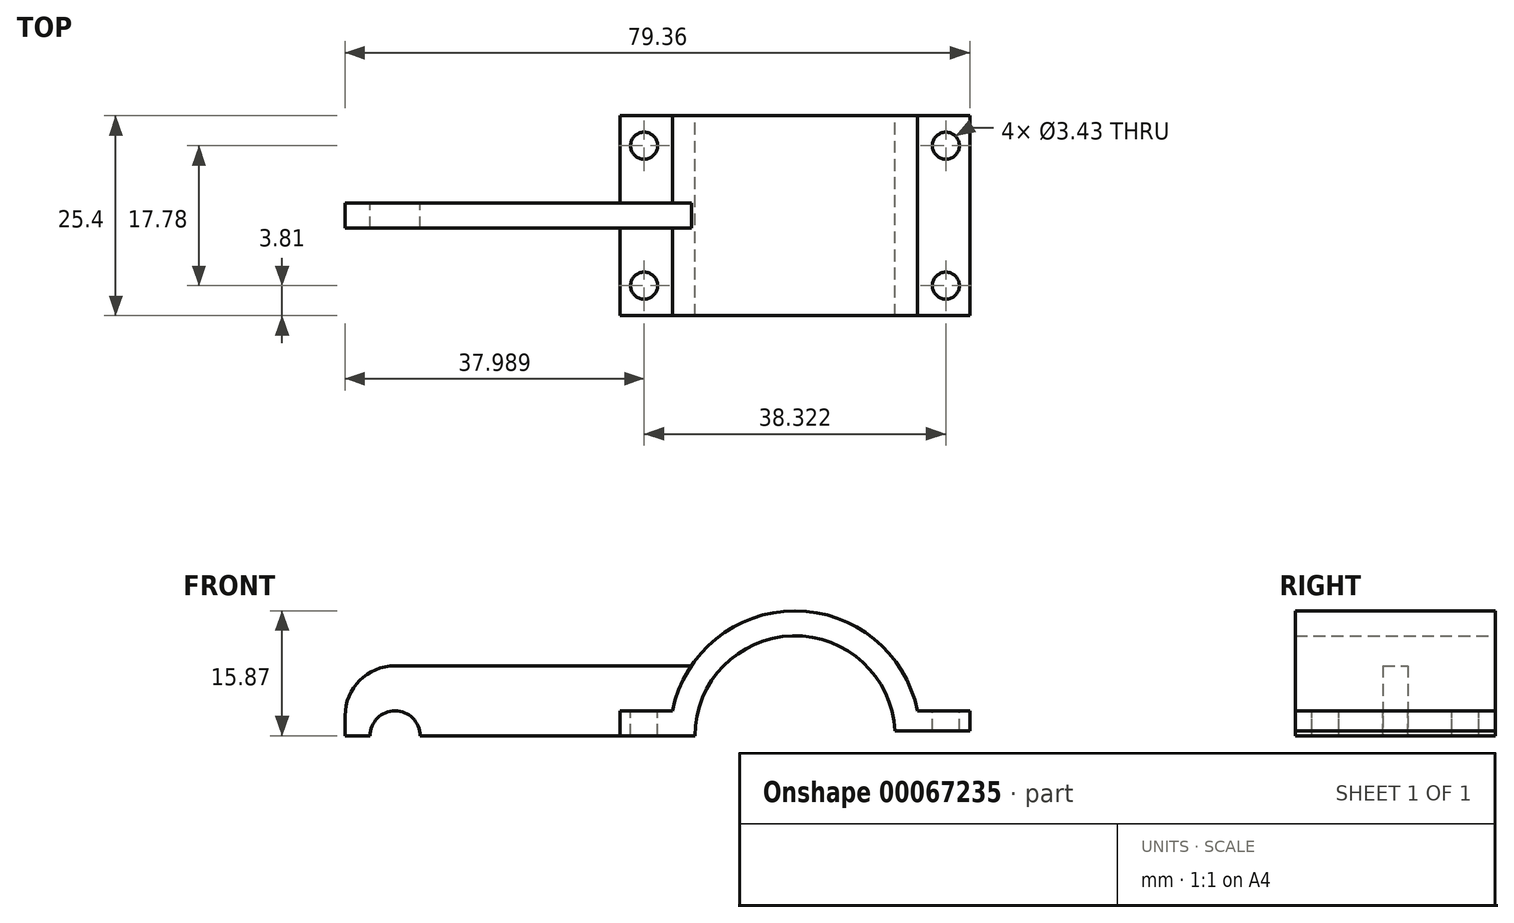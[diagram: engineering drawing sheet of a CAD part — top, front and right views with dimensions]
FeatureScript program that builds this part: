
annotation { "Feature Type Name" : "Feature", "Feature Type Description" : "" }
export const myFeature = defineFeature(function(context is Context, id is Id, definition is map)
    precondition{}
    {
        {
            var Q0;
            Q0=qCreatedBy(makeId("Front.planeOp"),FACE);
            var sketch = newSketch(context, id + "F0", { "sketchPlane" : qUnion([Q0])});
            skArc(sketch, "E0", {"start": v(12.68, 0.64) * mm, "mid": v(0, 12.7) * mm, "end": v(-12.68, 0.63) * mm});
            skArc(sketch, "E1", {"start": v(15.55, 3.18) * mm, "mid": v(0, 15.88) * mm, "end": v(-15.55, 3.18) * mm});
            skLineSegment(sketch, "E2", {"start": v(-15.55, 3.18) * mm, "end": v(-22.2, 3.17) * mm});
            skLineSegment(sketch, "E3", {"start": v(-22.2, 3.18) * mm, "end": v(-22.2, 0.63) * mm});
            skLineSegment(sketch, "E4.MirrorCS", {"start": v(15.55, 3.18) * mm, "end": v(22.2, 3.17) * mm});
            skLineSegment(sketch, "E5.MirrorCS", {"start": v(22.2, 3.18) * mm, "end": v(22.2, 0.63) * mm});
            skPoint(sketch, "E6.end.orphan", {"position": v(-15.88, 0) * mm});
            skPoint(sketch, "E7.orphan", {"position": v(-12.7, 0) * mm});
            skPoint(sketch, "E8.orphan", {"position": v(-22.2, 0) * mm});
            skLineSegment(sketch, "E9.trimOffspring", {"start": v(12.68, 0.64) * mm, "end": v(22.2, 0.64) * mm});
            skPoint(sketch, "E10.MirrorCS.end.orphan", {"position": v(15.88, 0) * mm});
            skPoint(sketch, "E11.orphan", {"position": v(22.2, 0) * mm});
            skLineSegment(sketch, "E12", {"start": v(-22.2, 0.63) * mm, "end": v(-22.2, 0) * mm});
            skArc(sketch, "E13", {"start": v(-12.68, 0.63) * mm, "mid": v(-12.7, 0.32) * mm, "end": v(-12.7, 0) * mm});
            skLineSegment(sketch, "E14", {"start": v(-22.2, 0) * mm, "end": v(-12.7, 0) * mm});
            skSolve(sketch);
        }
        {
            var Q0;
            Q0=makeQuery(id+"F0.imprint","IMPRINT",FACE,{"disambiguationData":[TD([[makeQuery(id+"F0.imprint","IMPRINT",EDGE,{"derivedFrom":sQuery(id+"F0.wireOp",EDGE,"E0")}),-1.0]])]});
            extrude(context, id + "F1", {"entities" : qUnion([Q0]), "depth" : 25.4 * mm, "symmetric" : true});
        }
        {
            var Q0;
            Q0=qCreatedBy(makeId("Front.planeOp"),FACE);
            var sketch = newSketch(context, id + "F2", { "sketchPlane" : qUnion([Q0])});
            skArc(sketch, "E15.0", {"start": v(-13.15, 8.9) * mm, "mid": v(-14.63, 6.15) * mm, "end": v(-15.55, 3.18) * mm});
            skLineSegment(sketch, "E16", {"start": v(-13.15, 8.9) * mm, "end": v(-50.8, 8.9) * mm});
            skLineSegment(sketch, "E17", {"start": v(-57.15, 2.54) * mm, "end": v(-57.15, 0) * mm});
            skPoint(sketch, "E18.0", {"position": v(-22.2, 0) * mm});
            skLineSegment(sketch, "E19", {"start": v(-57.15, 0) * mm, "end": v(-53.98, 0) * mm});
            skArc(sketch, "E20", {"start": v(-47.63, 0) * mm, "mid": v(-50.8, 3.18) * mm, "end": v(-53.98, 0) * mm});
            skPoint(sketch, "E21.visualSharp", {"position": v(-57.15, 8.9) * mm});
            skArc(sketch, "E21.filletArc", {"start": v(-50.8, 8.9) * mm, "mid": v(-55.3, 7.03) * mm, "end": v(-57.15, 2.54) * mm});
            skLineSegment(sketch, "E22.trimOffspring", {"start": v(-47.63, 0) * mm, "end": v(-22.2, 0) * mm});
            skPoint(sketch, "E23.orphan", {"position": v(15.55, 3.18) * mm});
            skLineSegment(sketch, "E24", {"start": v(-22.2, 0) * mm, "end": v(-22.2, 3.18) * mm});
            skLineSegment(sketch, "E25", {"start": v(-15.55, 3.18) * mm, "end": v(-22.2, 3.18) * mm});
            skSolve(sketch);
        }
        {
            var Q0;
            Q0=makeQuery(id+"F2.imprint","IMPRINT",FACE,{"disambiguationData":[TD([[makeQuery(id+"F2.imprint","IMPRINT",EDGE,{"derivedFrom":sQuery(id+"F2.wireOp",EDGE,"E15.0")}),-1.0]])]});
            extrude(context, id + "F3", {"entities" : qUnion([Q0]), "operationType" : NewBodyOperationType.ADD, "depth" : 3.17 * mm, "symmetric" : true});
        }
        {
            var Q0;
            Q0=makeQuery(id+"F1.opExtrude","SWEPT_FACE",FACE,{"disambiguationData":[OSD([sQuery(id+"F0.wireOp",EDGE,"E4.MirrorCS")])]});
            var sketch = newSketch(context, id + "F4", { "sketchPlane" : qUnion([Q0])});
            skCircle(sketch, "E26", {"center": v(19.16, 8.9) * mm, "radius": 1.71 * mm});
            skCircle(sketch, "E27", {"center": v(19.16, -8.9) * mm, "radius": 1.71 * mm});
            skCircle(sketch, "E28.MirrorC", {"center": v(-19.16, -8.9) * mm, "radius": 1.71 * mm});
            skCircle(sketch, "E29.MirrorC", {"center": v(-19.16, 8.9) * mm, "radius": 1.71 * mm});
            skSolve(sketch);
        }
        {
            var Q0;
            Q0 = qSketchRegion(id + "F4", true);
            var Q1;
            Q1=makeQuery(id+"Fb1grqasLBWUTu8_1.opPattern","COPY",FACE,{"derivedFrom":makeQuery(id+"F1.opExtrude","SWEPT_FACE",FACE,{"disambiguationData":[OSD([sQuery(id+"F0.wireOp",EDGE,"E4.MirrorCS")])]}),"instanceName":"1"});
            extrude(context, id + "F5", {"entities" : qUnion([Q0]), "operationType" : NewBodyOperationType.REMOVE, "oppositeDirection" : true, "endBoundEntityFace" : qUnion([Q1]), "depth" : 25.4 * mm});
        }
    });
